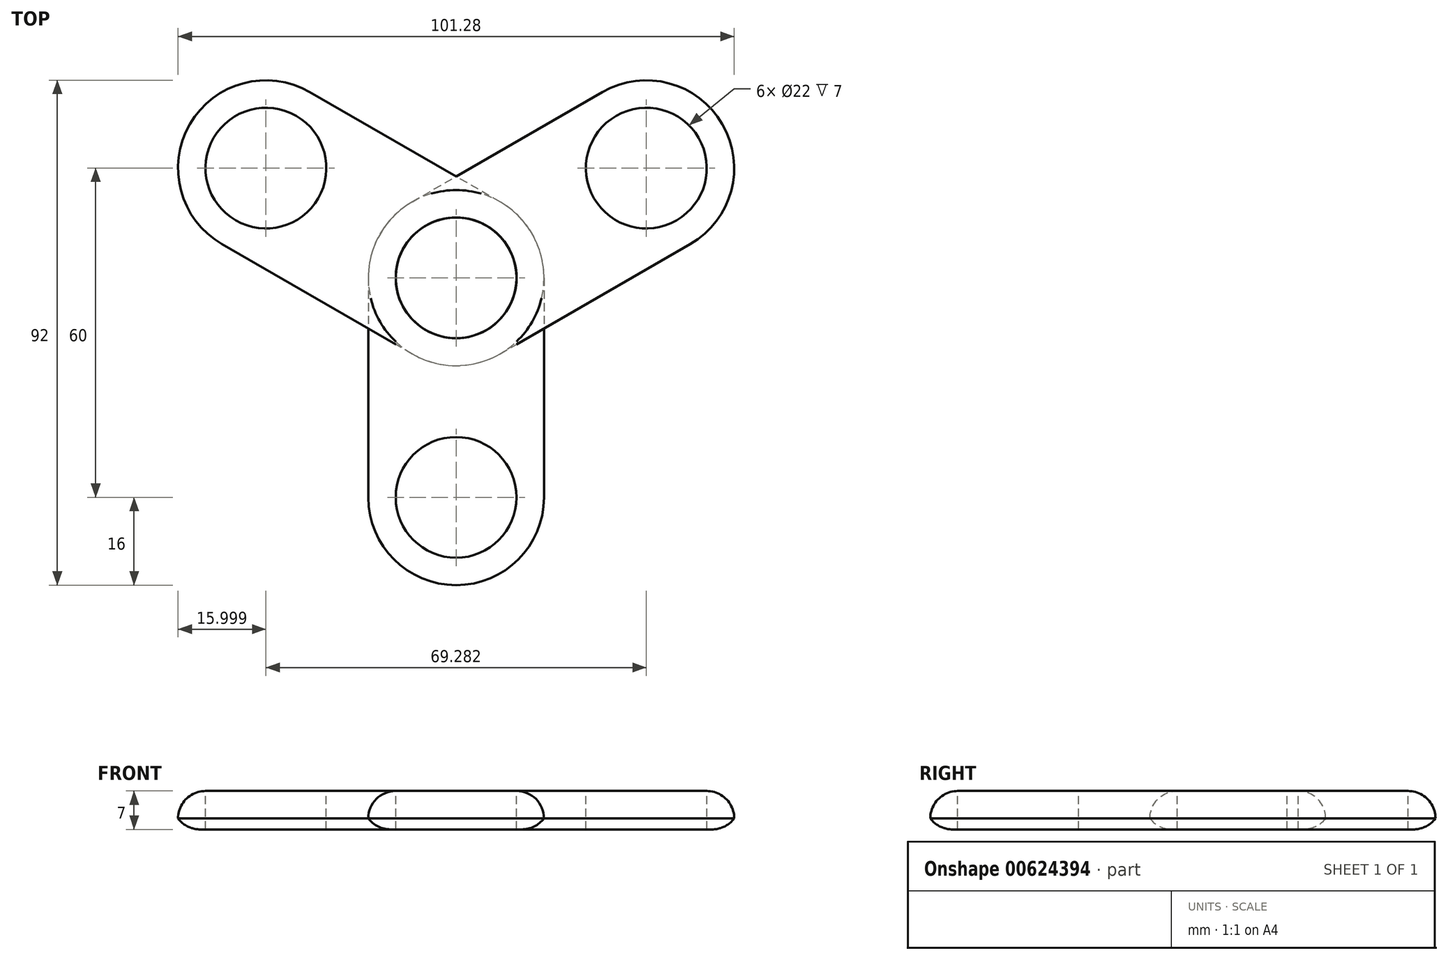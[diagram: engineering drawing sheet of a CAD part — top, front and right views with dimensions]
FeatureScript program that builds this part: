
annotation { "Feature Type Name" : "Feature", "Feature Type Description" : "" }
export const myFeature = defineFeature(function(context is Context, id is Id, definition is map)
    precondition{}
    {
        {
            var Q0;
            Q0=qCreatedBy(makeId("Top.planeOp"),FACE);
            var sketch = newSketch(context, id + "F0", { "sketchPlane" : qUnion([Q0])});
            skCircle(sketch, "E0", {"center": v(0, 0) * mm, "radius": 16 * mm});
            skCircle(sketch, "E1", {"center": v(0, -40) * mm, "radius": 16 * mm});
            skLineSegment(sketch, "E2", {"start": v(16, 0) * mm, "end": v(16, -40) * mm});
            skLineSegment(sketch, "E3", {"start": v(-16, 0) * mm, "end": v(-16, -40) * mm});
            skSolve(sketch);
        }
        {
            var Q0;
            Q0 = qSketchRegion(id + "F0", true);
            extrude(context, id + "F1", {"entities" : qUnion([Q0]), "depth" : 7 * mm, "offsetDistance" : 25 * mm});
        }
        {
            var Q0;
            Q0=makeQuery(id+"F1.opExtrude","CAP_FACE",FACE,{"disambiguationData":[OSD([sQuery(id+"F0.wireOp",EDGE,"E0"),sQuery(id+"F0.wireOp",EDGE,"E1"),sQuery(id+"F0.wireOp",EDGE,"E2"),sQuery(id+"F0.wireOp",EDGE,"E3")])],"isStart":false});
            var sketch = newSketch(context, id + "F2", { "sketchPlane" : qUnion([Q0])});
            skCircle(sketch, "E4", {"center": v(0, 0) * mm, "radius": 11 * mm});
            skCircle(sketch, "E5", {"center": v(0, -40) * mm, "radius": 11 * mm});
            skSolve(sketch);
        }
        {
            var Q0;
            Q0 = qSketchRegion(id + "F2", true);
            extrude(context, id + "F3", {"entities" : qUnion([Q0]), "operationType" : NewBodyOperationType.REMOVE, "endBound" : BoundingType.THROUGH_ALL, "oppositeDirection" : true, "depth" : 25 * mm, "offsetDistance" : 25 * mm});
        }
        {
            var Q0;
            Q0=qCreatedBy(makeId("Front.planeOp"),FACE);
            var sketch = newSketch(context, id + "F4", { "sketchPlane" : qUnion([Q0])});
            skLineSegment(sketch, "E6", {"start": v(0, 0) * mm, "end": v(0, 38) * mm});
            skSolve(sketch);
        }
        {
            var Q0;
            Q0=makeQuery(id+"F1.opExtrude","SWEPT_BODY",BODY,{"disambiguationData":[OSD([sQuery(id+"F0.wireOp",EDGE,"E0"),sQuery(id+"F0.wireOp",EDGE,"E1"),sQuery(id+"F0.wireOp",EDGE,"E2"),sQuery(id+"F0.wireOp",EDGE,"E3")])]});
            var Q1;
            Q1=sQuery(id+"F4.wireOp",EDGE,"E6");
            circularPattern(context, id + "F5", {"entities" : qUnion([Q0]), "axis" : qUnion([Q1]), "angle" : 360 * degree, "instanceCount" : 3, "equalSpace" : true});
        }
        {
            var Q0;
            Q0=makeQuery(id+"F5.opPattern","COPY",EDGE,{"derivedFrom":makeQuery(id+"F1.opExtrude","CAP_EDGE",EDGE,{"disambiguationData":[OSD([sQuery(id+"F0.wireOp",EDGE,"E3")])],"isStart":false}),"instanceName":"2"});
            var Q1;
            Q1=makeQuery(id+"F5.opPattern","COPY",EDGE,{"derivedFrom":makeQuery(id+"F1.opExtrude","CAP_EDGE",EDGE,{"disambiguationData":[OSD([sQuery(id+"F0.wireOp",EDGE,"E2")])],"isStart":false}),"instanceName":"1"});
            var Q2;
            Q2=makeQuery(id+"F1.opExtrude","CAP_EDGE",EDGE,{"disambiguationData":[OSD([sQuery(id+"F0.wireOp",EDGE,"E2")])],"isStart":false});
            fillet(context, id + "F6", {"entities" : qUnion([Q0, Q1, Q2]), "radius" : 5 * mm, "tangentPropagation" : true, "allowEdgeOverflow" : false});
        }
        {
            var Q0;
            {var subQ0=sQuery(id+"F0.wireOp",EDGE,"E1");Q0=makeQuery(id+"F6.opFillet","BLEND_EDGE",EDGE,{"blendedFrom":[makeQuery(id+"F5.opPattern","COPY",EDGE,{"derivedFrom":makeQuery(id+"F1.opExtrude","CAP_EDGE",EDGE,{"disambiguationData":[OSD([subQ0])],"isStart":false}),"instanceName":"1"}),makeQuery(id+"F5.opPattern","COPY",FACE,{"derivedFrom":makeQuery(id+"F1.opExtrude","SWEPT_FACE",FACE,{"disambiguationData":[OSD([subQ0])]}),"instanceName":"1"})],"blendedInto":[makeQuery(id+"F5.opPattern","COPY",FACE,{"derivedFrom":makeQuery(id+"F1.opExtrude","SWEPT_FACE",FACE,{"disambiguationData":[OSD([subQ0])]}),"instanceName":"1"})]});}
            var Q1;
            Q1=makeQuery(id+"F5.opPattern","COPY",EDGE,{"derivedFrom":makeQuery(id+"F1.opExtrude","CAP_EDGE",EDGE,{"disambiguationData":[OSD([sQuery(id+"F0.wireOp",EDGE,"E1")])],"isStart":true}),"instanceName":"1"});
            var Q2;
            Q2=makeQuery(id+"F1.opExtrude","CAP_EDGE",EDGE,{"disambiguationData":[OSD([sQuery(id+"F0.wireOp",EDGE,"E1")])],"isStart":true});
            var Q3;
            Q3=makeQuery(id+"F5.opPattern","COPY",EDGE,{"derivedFrom":makeQuery(id+"F1.opExtrude","CAP_EDGE",EDGE,{"disambiguationData":[OSD([sQuery(id+"F0.wireOp",EDGE,"E1")])],"isStart":true}),"instanceName":"2"});
            fillet(context, id + "F7", {"entities" : qUnion([Q0, Q1, Q2, Q3]), "radius" : 5 * mm, "tangentPropagation" : true, "allowEdgeOverflow" : false});
        }
    });
